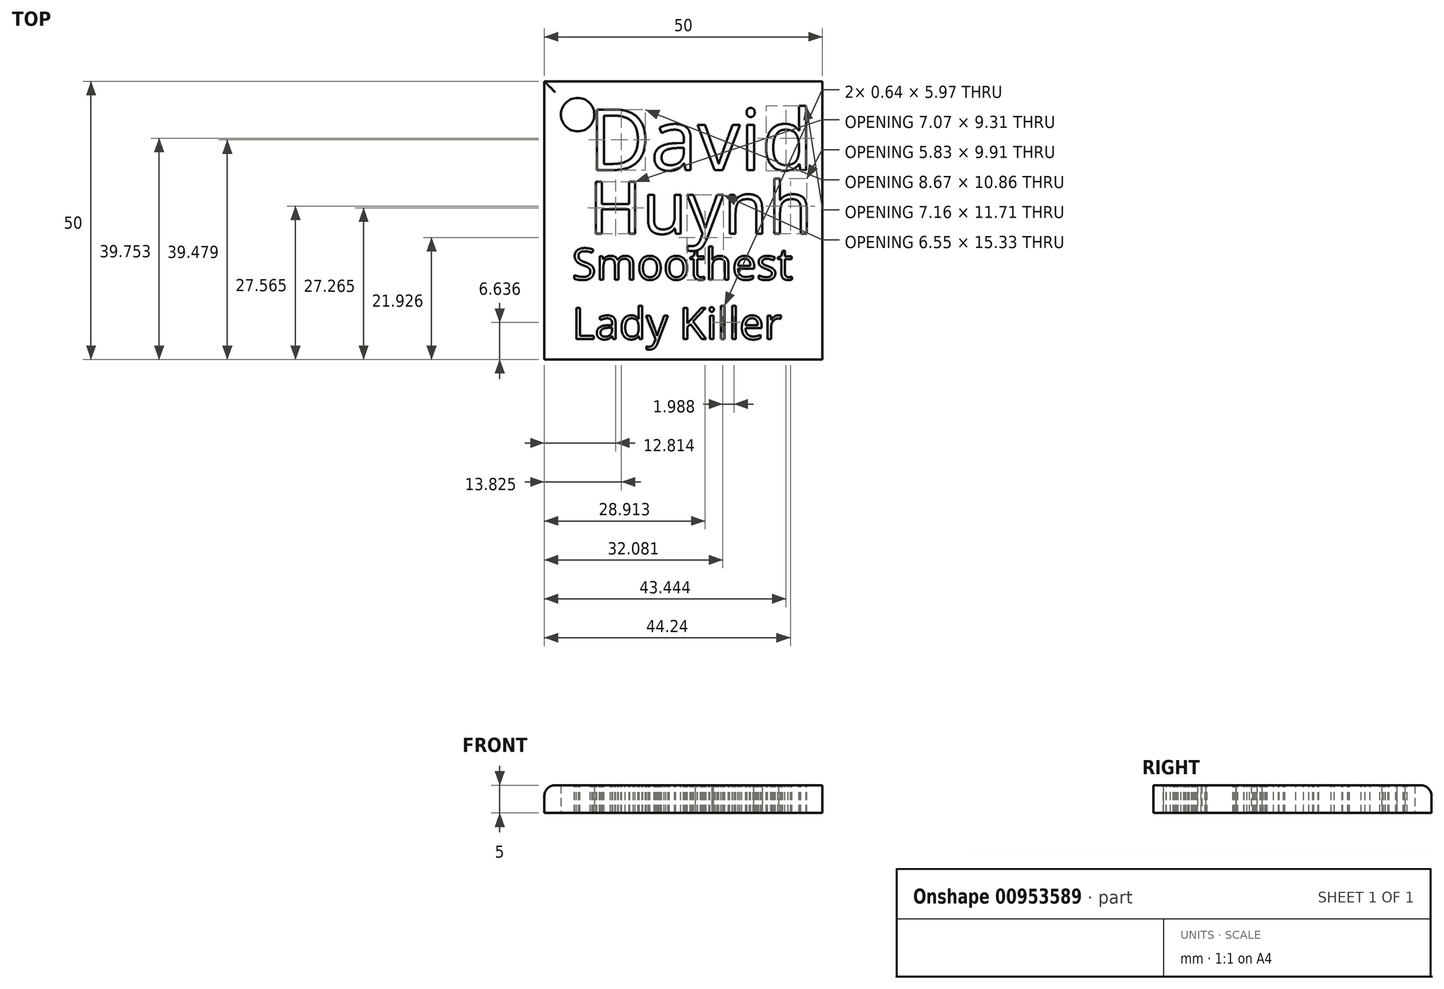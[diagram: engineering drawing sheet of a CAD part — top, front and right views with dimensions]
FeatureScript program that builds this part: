
annotation { "Feature Type Name" : "Feature", "Feature Type Description" : "" }
export const myFeature = defineFeature(function(context is Context, id is Id, definition is map)
    precondition{}
    {
        {
            var Q0;
            Q0=qCreatedBy(makeId("Top.planeOp"),FACE);
            var sketch = newSketch(context, id + "F0", { "sketchPlane" : qUnion([Q0])});
            skLineSegment(sketch, "E0.bottom", {"start": v(0, 0) * mm, "end": v(50, 0) * mm});
            skLineSegment(sketch, "E0.top", {"start": v(0, -50) * mm, "end": v(50, -50) * mm});
            skLineSegment(sketch, "E0.left", {"start": v(0, 0) * mm, "end": v(0, -50) * mm});
            skLineSegment(sketch, "E0.right", {"start": v(50, 0) * mm, "end": v(50, -50) * mm});
            skCircle(sketch, "E1", {"center": v(6, -6) * mm, "radius": 3 * mm});
            skSolve(sketch);
        }
        {
            var Q0;
            Q0=makeQuery(id+"F0.imprint","IMPRINT",FACE,{"disambiguationData":[TD([[makeQuery(id+"F0.imprint","IMPRINT",EDGE,{"derivedFrom":sQuery(id+"F0.wireOp",EDGE,"E0.bottom")}),-1.0]])]});
            extrude(context, id + "F1", {"entities" : qUnion([Q0]), "depth" : 5 * mm, "offsetDistance" : 25 * mm});
        }
        {
            var Q0;
            {var subQ118=sQuery(id+"F0.wireOp",EDGE,"E0.top");var subQ119=makeQuery(id+"F1.opExtrude","SWEPT_FACE",FACE,{"disambiguationData":[OSD([subQ118])]});var subQ122=sQuery(id+"F0.wireOp",EDGE,"E0.right");var subQ135=sQuery(id+"F0.wireOp",EDGE,"E1");var subQ237=sQuery(id+"F0.wireOp",EDGE,"E0.bottom");var subQ239=sQuery(id+"F0.wireOp",EDGE,"E0.left");Q0=makeQuery(id+"F7.boolean.opBoolean","SPLIT",FACE,{"disambiguationData":[TD([subQ119])],"derivedFrom":makeQuery(id+"F4.boolean.opBoolean","SPLIT",FACE,{"disambiguationData":[TD([makeQuery(id+"F1.opExtrude","SWEPT_FACE",FACE,{"disambiguationData":[OSD([subQ237])]})])],"derivedFrom":makeQuery(id+"F1.opExtrude","CAP_FACE",FACE,{"disambiguationData":[OSD([subQ237,subQ118,subQ239,subQ122,subQ135])],"isStart":false})})});}
            var sketch = newSketch(context, id + "F2", { "sketchPlane" : qUnion([Q0])});
            skText(sketch, "E2", { "text": "Huynh", "fontName": "OpenSans-Regular.ttf"});
            const initialGuessF2  = {"E2": [0.008, -0.02739, 1, 0, 0.00939]};
            skSetInitialGuess(sketch, initialGuessF2);
            skSolve(sketch);
        }
        {
            var Q0;
            {var subQ0=sQuery(id+"F0.wireOp",EDGE,"E0.left");var subQ1=sQuery(id+"F0.wireOp",EDGE,"E0.bottom");var subQ2=sQuery(id+"F0.wireOp",EDGE,"E1");var subQ3=sQuery(id+"F0.wireOp",EDGE,"E0.right");var subQ4=sQuery(id+"F0.wireOp",EDGE,"E0.top");Q0=makeQuery(id+"F7.boolean.opBoolean","SPLIT",FACE,{"disambiguationData":[TD([makeQuery(id+"F1.opExtrude","SWEPT_FACE",FACE,{"disambiguationData":[OSD([subQ4])]})])],"derivedFrom":makeQuery(id+"F1.opExtrude","CAP_FACE",FACE,{"disambiguationData":[OSD([subQ1,subQ4,subQ0,subQ3,subQ2])],"isStart":false})});}
            var sketch = newSketch(context, id + "F3", { "sketchPlane" : qUnion([Q0])});
            skText(sketch, "E3", { "text": "Smoothest \nLady Killer", "fontName": "OpenSans-Regular.ttf"});
            const initialGuessF3  = {"E3": [0.005, -0.03566, 1, 0, 0.00566]};
            skSetInitialGuess(sketch, initialGuessF3);
            skSolve(sketch);
        }
        {
            var Q0;
            Q0=makeQuery(id+"F2.imprint","IMPRINT",FACE,{"disambiguationData":[TD([[makeQuery(id+"F2.imprint","IMPRINT",EDGE,{"derivedFrom":sQuery(id+"F2.wireOp",EDGE,"E2.sketch_text.stroke-0")}),-1.0]])]});
            var Q1;
            Q1=makeQuery(id+"F2.imprint","IMPRINT",FACE,{"disambiguationData":[TD([[makeQuery(id+"F2.imprint","IMPRINT",EDGE,{"derivedFrom":sQuery(id+"F2.wireOp",EDGE,"E2.sketch_text.stroke-12")}),-1.0]])]});
            var Q2;
            Q2=makeQuery(id+"F2.imprint","IMPRINT",FACE,{"disambiguationData":[TD([[makeQuery(id+"F2.imprint","IMPRINT",EDGE,{"derivedFrom":sQuery(id+"F2.wireOp",EDGE,"E2.sketch_text.stroke-29")}),-1.0]])]});
            var Q3;
            Q3=makeQuery(id+"F2.imprint","IMPRINT",FACE,{"disambiguationData":[TD([[makeQuery(id+"F2.imprint","IMPRINT",EDGE,{"derivedFrom":sQuery(id+"F2.wireOp",EDGE,"E2.sketch_text.stroke-45")}),-1.0]])]});
            var Q4;
            Q4=makeQuery(id+"F2.imprint","IMPRINT",FACE,{"disambiguationData":[TD([[makeQuery(id+"F2.imprint","IMPRINT",EDGE,{"derivedFrom":sQuery(id+"F2.wireOp",EDGE,"E2.sketch_text.stroke-62")}),-1.0]])]});
            extrude(context, id + "F4", {"entities" : qUnion([Q0, Q1, Q2, Q3, Q4]), "operationType" : NewBodyOperationType.REMOVE, "endBound" : BoundingType.THROUGH_ALL, "oppositeDirection" : true, "depth" : 25 * mm, "offsetDistance" : 25 * mm});
        }
        {
            var Q0;
            Q0=makeQuery(id+"F1.opExtrude","CAP_EDGE",EDGE,{"disambiguationData":[OSD([sQuery(id+"F0.wireOp",EDGE,"E0.left")])],"isStart":false});
            var Q1;
            Q1=makeQuery(id+"F1.opExtrude","CAP_EDGE",EDGE,{"disambiguationData":[OSD([sQuery(id+"F0.wireOp",EDGE,"E0.bottom")])],"isStart":false});
            fillet(context, id + "F5", {"entities" : qUnion([Q0, Q1]), "radius" : 2 * mm, "tangentPropagation" : true, "allowEdgeOverflow" : false});
        }
        {
            var Q0;
            {var subQ0=sQuery(id+"F0.wireOp",EDGE,"E0.left");var subQ1=sQuery(id+"F0.wireOp",EDGE,"E1");var subQ2=sQuery(id+"F0.wireOp",EDGE,"E0.bottom");var subQ3=sQuery(id+"F0.wireOp",EDGE,"E0.right");var subQ4=sQuery(id+"F0.wireOp",EDGE,"E0.top");Q0=makeQuery(id+"F4.boolean.opBoolean","SPLIT",FACE,{"disambiguationData":[TD([makeQuery(id+"F1.opExtrude","SWEPT_FACE",FACE,{"disambiguationData":[OSD([subQ2])]})])],"derivedFrom":makeQuery(id+"F1.opExtrude","CAP_FACE",FACE,{"disambiguationData":[OSD([subQ2,subQ4,subQ0,subQ3,subQ1])],"isStart":false})});}
            var sketch = newSketch(context, id + "F6", { "sketchPlane" : qUnion([Q0])});
            skText(sketch, "E4", { "text": "David", "fontName": "OpenSans-Regular.ttf"});
            const initialGuessF6  = {"E4": [0.008, -0.01595, 1, 0, 0.01095]};
            skSetInitialGuess(sketch, initialGuessF6);
            skSolve(sketch);
        }
        {
            var Q0;
            Q0 = qSketchRegion(id + "F6", true);
            extrude(context, id + "F7", {"entities" : qUnion([Q0]), "operationType" : NewBodyOperationType.REMOVE, "endBound" : BoundingType.THROUGH_ALL, "oppositeDirection" : true, "depth" : 25 * mm, "offsetDistance" : 25 * mm});
        }
        {
            var Q0;
            Q0 = qSketchRegion(id + "F3", true);
            extrude(context, id + "F8", {"entities" : qUnion([Q0]), "operationType" : NewBodyOperationType.REMOVE, "endBound" : BoundingType.THROUGH_ALL, "oppositeDirection" : true, "depth" : 25 * mm, "offsetDistance" : 25 * mm});
        }
    });
